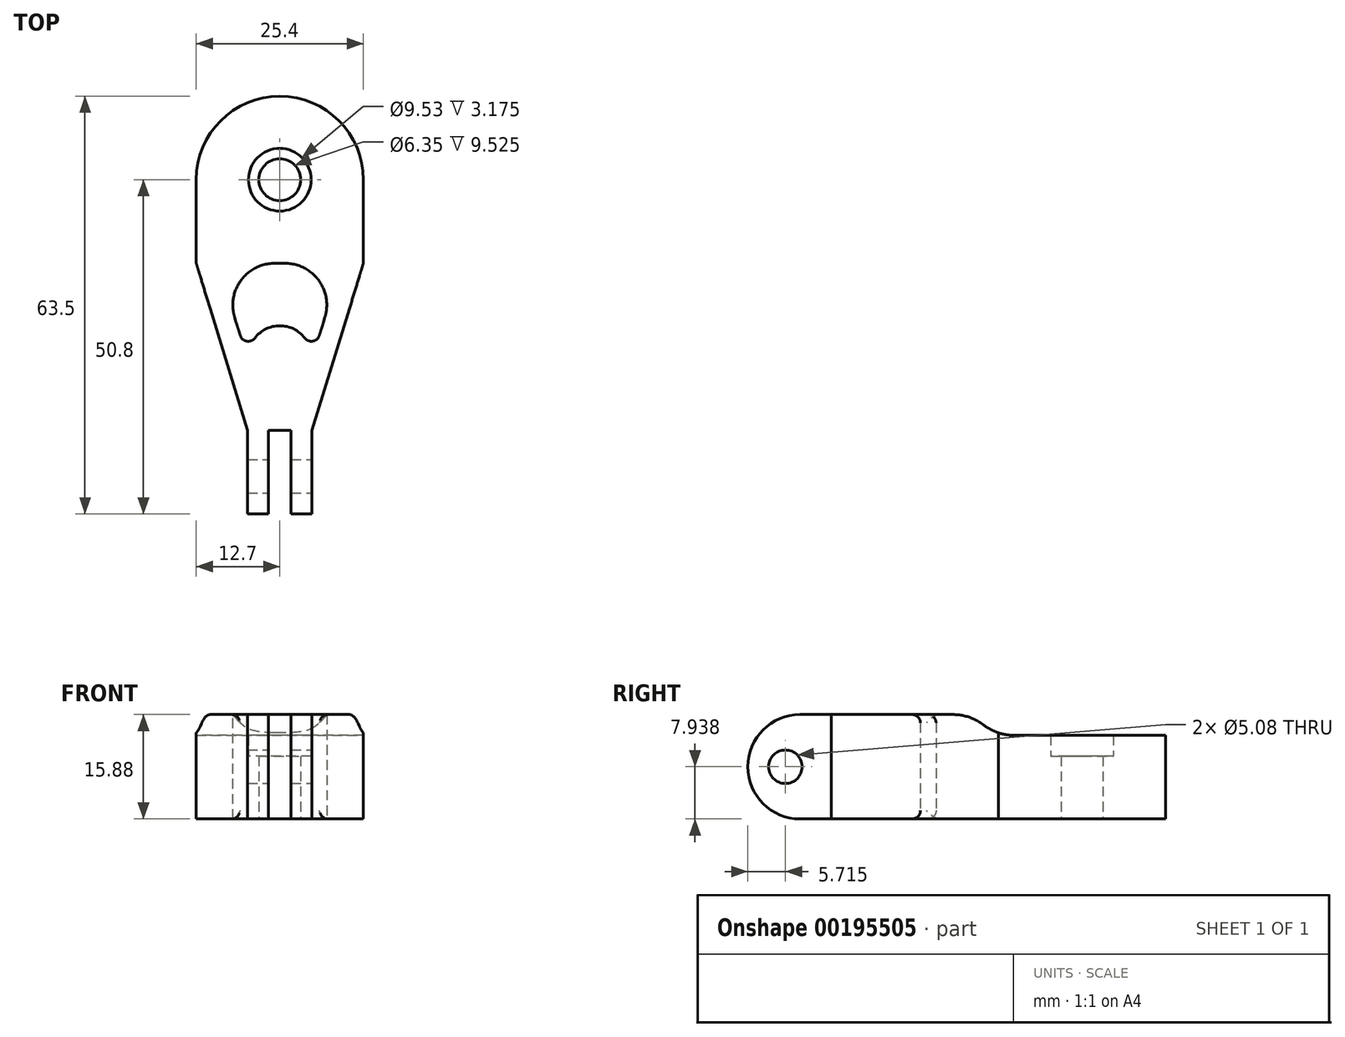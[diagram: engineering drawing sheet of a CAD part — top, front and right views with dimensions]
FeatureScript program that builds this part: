
annotation { "Feature Type Name" : "Feature", "Feature Type Description" : "" }
export const myFeature = defineFeature(function(context is Context, id is Id, definition is map)
    precondition{}
    {
        {
            var Q0;
            Q0=qCreatedBy(makeId("Top.planeOp"),FACE);
            var sketch = newSketch(context, id + "F0", { "sketchPlane" : qUnion([Q0])});
            skCircle(sketch, "E0", {"center": v(0, 0) * mm, "radius": 4.76 * mm});
            skCircle(sketch, "E1", {"center": v(0, 0) * mm, "radius": 12.7 * mm});
            skLineSegment(sketch, "E2.bottom", {"start": v(-12.7, 0) * mm, "end": v(12.7, 0) * mm});
            skLineSegment(sketch, "E2.top", {"start": v(-12.7, -50.8) * mm, "end": v(12.7, -50.8) * mm});
            skLineSegment(sketch, "E2.left", {"start": v(-12.7, 0) * mm, "end": v(-12.7, -50.8) * mm});
            skLineSegment(sketch, "E2.right", {"start": v(12.7, 0) * mm, "end": v(12.7, -50.8) * mm});
            skSolve(sketch);
        }
        {
            var Q0;
            {var subQ0=sQuery(id+"F0.wireOp",EDGE,"E2.bottom");var subQ1=sQuery(id+"F0.wireOp",EDGE,"E0");var subQ5=makeQuery(id+"F0.imprint","INTERSECT",VERTEX,{"disambiguationData":[OD(0.0)],"derivedFrom":[subQ1,subQ0]});Q0=makeQuery(id+"F0.imprint","IMPRINT",FACE,{"disambiguationData":[TD([[makeQuery(id+"F0.imprint","IMPRINT",EDGE,{"disambiguationData":[TD([[subQ5,1.0]])],"derivedFrom":subQ1}),-1.0]])]});}
            var Q1;
            {var subQ0=sQuery(id+"F0.wireOp",EDGE,"E2.bottom");var subQ1=sQuery(id+"F0.wireOp",EDGE,"E0");var subQ5=makeQuery(id+"F0.imprint","INTERSECT",VERTEX,{"disambiguationData":[OD(0.0)],"derivedFrom":[subQ1,subQ0]});Q1=makeQuery(id+"F0.imprint","IMPRINT",FACE,{"disambiguationData":[TD([[makeQuery(id+"F0.imprint","IMPRINT",EDGE,{"disambiguationData":[TD([[subQ5,-1.0]])],"derivedFrom":subQ1}),-1.0]])]});}
            var Q2;
            Q2=makeQuery(id+"F0.imprint","IMPRINT",FACE,{"disambiguationData":[TD([[makeQuery(id+"F0.imprint","IMPRINT",EDGE,{"derivedFrom":sQuery(id+"F0.wireOp",EDGE,"E2.top")}),1.0]])]});
            extrude(context, id + "F1", {"entities" : qUnion([Q0, Q1, Q2]), "depth" : 15.88 * mm});
        }
        {
            var Q0;
            Q0=qCreatedBy(makeId("Right.planeOp"),FACE);
            var sketch = newSketch(context, id + "F2", { "sketchPlane" : qUnion([Q0])});
            skLineSegment(sketch, "E3", {"start": v(12.7, 12.7) * mm, "end": v(-12.7, 12.7) * mm});
            skLineSegment(sketch, "E4", {"start": v(-12.7, 12.7) * mm, "end": v(-40.44, 32.12) * mm});
            skLineSegment(sketch, "E5", {"start": v(-40.44, 32.12) * mm, "end": v(12.7, 32.12) * mm});
            skLineSegment(sketch, "E6", {"start": v(12.7, 32.12) * mm, "end": v(12.7, 12.7) * mm});
            skSolve(sketch);
        }
        {
            var Q0;
            Q0=makeQuery(id+"F2.imprint","IMPRINT",FACE,{"disambiguationData":[TD([[makeQuery(id+"F2.imprint","IMPRINT",EDGE,{"derivedFrom":sQuery(id+"F2.wireOp",EDGE,"E3")}),-1.0]])]});
            extrude(context, id + "F3", {"entities" : qUnion([Q0]), "operationType" : NewBodyOperationType.REMOVE, "endBound" : BoundingType.SYMMETRIC, "oppositeDirection" : true, "depth" : 25.4 * mm});
        }
        {
            var Q0;
            Q0=makeQuery(id+"F1.opExtrude","CAP_FACE",FACE,{"disambiguationData":[OSD([sQuery(id+"F0.wireOp",EDGE,"E0"),sQuery(id+"F0.wireOp",EDGE,"E1"),sQuery(id+"F0.wireOp",EDGE,"E2.top"),sQuery(id+"F0.wireOp",EDGE,"E2.left"),sQuery(id+"F0.wireOp",EDGE,"E2.right")])],"isStart":false});
            var sketch = newSketch(context, id + "F4", { "sketchPlane" : qUnion([Q0])});
            skLineSegment(sketch, "E7.bottom", {"start": v(-4.9, -38.1) * mm, "end": v(-1.73, -38.1) * mm});
            skLineSegment(sketch, "E7.top", {"start": v(-4.9, -50.8) * mm, "end": v(-1.73, -50.8) * mm});
            skLineSegment(sketch, "E7.left", {"start": v(-4.9, -38.1) * mm, "end": v(-4.9, -50.8) * mm});
            skLineSegment(sketch, "E7.right", {"start": v(-1.73, -38.1) * mm, "end": v(-1.73, -50.8) * mm});
            skLineSegment(sketch, "E8.bottom", {"start": v(1.73, -38.1) * mm, "end": v(4.9, -38.1) * mm});
            skLineSegment(sketch, "E8.top", {"start": v(1.73, -50.8) * mm, "end": v(4.9, -50.8) * mm});
            skLineSegment(sketch, "E8.left", {"start": v(1.73, -38.1) * mm, "end": v(1.73, -50.8) * mm});
            skLineSegment(sketch, "E8.right", {"start": v(4.9, -38.1) * mm, "end": v(4.9, -50.8) * mm});
            skLineSegment(sketch, "E9.0.0", {"start": v(12.7, -50.8) * mm, "end": v(12.7, -17.23) * mm});
            skLineSegment(sketch, "E9.0.1", {"start": v(12.7, -17.23) * mm, "end": v(-12.7, -17.23) * mm});
            skLineSegment(sketch, "E9.0.2", {"start": v(-12.7, -17.23) * mm, "end": v(-12.7, -50.8) * mm});
            skLineSegment(sketch, "E9.0.3", {"start": v(-12.7, -50.8) * mm, "end": v(12.7, -50.8) * mm});
            skLineSegment(sketch, "E10", {"start": v(-1.73, -38.1) * mm, "end": v(1.73, -38.1) * mm});
            skLineSegment(sketch, "E11", {"start": v(4.9, -38.1) * mm, "end": v(12.7, -38.1) * mm});
            skLineSegment(sketch, "E12", {"start": v(-4.9, -38.1) * mm, "end": v(-12.7, -38.1) * mm});
            skSolve(sketch);
        }
        {
            var Q0;
            {var subQ2=sQuery(id+"F4.wireOp",EDGE,"E7.left");Q0=makeQuery(id+"F4.imprint","IMPRINT",FACE,{"disambiguationData":[TD([[makeQuery(id+"F4.imprint","IMPRINT",EDGE,{"derivedFrom":subQ2}),-1.0]])]});}
            var Q1;
            {var subQ2=sQuery(id+"F4.wireOp",EDGE,"E7.right");Q1=makeQuery(id+"F4.imprint","IMPRINT",FACE,{"disambiguationData":[TD([[makeQuery(id+"F4.imprint","IMPRINT",EDGE,{"derivedFrom":subQ2}),1.0]])]});}
            var Q2;
            {var subQ2=sQuery(id+"F4.wireOp",EDGE,"E8.right");Q2=makeQuery(id+"F4.imprint","IMPRINT",FACE,{"disambiguationData":[TD([[makeQuery(id+"F4.imprint","IMPRINT",EDGE,{"derivedFrom":subQ2}),1.0]])]});}
            extrude(context, id + "F5", {"entities" : qUnion([Q0, Q1, Q2]), "operationType" : NewBodyOperationType.REMOVE, "oppositeDirection" : true, "depth" : 25.4 * mm});
        }
        {
            var Q0;
            Q0=makeQuery(id+"F5.boolean.opBoolean","COPY",FACE,{"derivedFrom":makeQuery(id+"F5.opExtrude","SWEPT_FACE",FACE,{"disambiguationData":[OSD([sQuery(id+"F4.wireOp",EDGE,"E8.right")])]})});
            var sketch = newSketch(context, id + "F6", { "sketchPlane" : qUnion([Q0])});
            skCircle(sketch, "E13", {"center": v(-45.09, 7.94) * mm, "radius": 2.54 * mm});
            skSolve(sketch);
        }
        {
            var Q0;
            Q0=qSketchRegion(id+"F6",true);
            extrude(context, id + "F7", {"entities" : qUnion([Q0]), "operationType" : NewBodyOperationType.REMOVE, "oppositeDirection" : true, "depth" : 25.4 * mm});
        }
        {
            var Q0;
            {var subQ0=sQuery(id+"F0.wireOp",EDGE,"E2.top");Q0=makeQuery(id+"F5.boolean.opBoolean","SPLIT",EDGE,{"disambiguationData":[TD([makeQuery(id+"F5.opExtrude","SWEPT_FACE",FACE,{"disambiguationData":[OSD([sQuery(id+"F4.wireOp",EDGE,"E8.left")])]})])],"derivedFrom":makeQuery(id+"F1.opExtrude","CAP_EDGE",EDGE,{"disambiguationData":[OSD([subQ0])],"isStart":false})});}
            var Q1;
            {var subQ0=sQuery(id+"F0.wireOp",EDGE,"E2.top");Q1=makeQuery(id+"F5.boolean.opBoolean","SPLIT",EDGE,{"disambiguationData":[TD([makeQuery(id+"F5.opExtrude","SWEPT_FACE",FACE,{"disambiguationData":[OSD([sQuery(id+"F4.wireOp",EDGE,"E7.left")])]})])],"derivedFrom":makeQuery(id+"F1.opExtrude","CAP_EDGE",EDGE,{"disambiguationData":[OSD([subQ0])],"isStart":false})});}
            var Q2;
            {var subQ0=sQuery(id+"F0.wireOp",EDGE,"E2.top");Q2=makeQuery(id+"F5.boolean.opBoolean","SPLIT",EDGE,{"disambiguationData":[TD([makeQuery(id+"F5.opExtrude","SWEPT_FACE",FACE,{"disambiguationData":[OSD([sQuery(id+"F4.wireOp",EDGE,"E7.left")])]})])],"derivedFrom":makeQuery(id+"F1.opExtrude","CAP_EDGE",EDGE,{"disambiguationData":[OSD([subQ0])],"isStart":true})});}
            var Q3;
            {var subQ0=sQuery(id+"F0.wireOp",EDGE,"E2.top");Q3=makeQuery(id+"F5.boolean.opBoolean","SPLIT",EDGE,{"disambiguationData":[TD([makeQuery(id+"F5.opExtrude","SWEPT_FACE",FACE,{"disambiguationData":[OSD([sQuery(id+"F4.wireOp",EDGE,"E8.left")])]})])],"derivedFrom":makeQuery(id+"F1.opExtrude","CAP_EDGE",EDGE,{"disambiguationData":[OSD([subQ0])],"isStart":true})});}
            fillet(context, id + "F8", {"entities" : qUnion([Q0, Q1, Q2, Q3]), "radius" : 7.94 * mm, "tangentPropagation" : true, "allowEdgeOverflow" : false});
        }
        {
            var Q0;
            Q0=qCreatedBy(makeId("Top.planeOp"),FACE);
            var sketch = newSketch(context, id + "F9", { "sketchPlane" : qUnion([Q0])});
            skLineSegment(sketch, "E14.0.0", {"start": v(-1.73, -38.1) * mm, "end": v(-1.73, -42.86) * mm});
            skLineSegment(sketch, "E14.0.1", {"start": v(-1.73, -42.86) * mm, "end": v(-4.9, -42.86) * mm});
            skLineSegment(sketch, "E14.0.2", {"start": v(-4.9, -42.86) * mm, "end": v(-4.9, -38.1) * mm});
            skLineSegment(sketch, "E14.0.3", {"start": v(-4.9, -38.1) * mm, "end": v(-12.7, -38.1) * mm});
            skLineSegment(sketch, "E14.0.4", {"start": v(-12.7, -38.1) * mm, "end": v(-12.7, 0) * mm});
            skArc(sketch, "E14.0.5", {"start": v(-12.7, 0) * mm, "mid": v(0, 12.7) * mm, "end": v(12.7, 0) * mm});
            skLineSegment(sketch, "E14.0.6", {"start": v(12.7, 0) * mm, "end": v(12.7, -38.1) * mm});
            skLineSegment(sketch, "E14.0.7", {"start": v(12.7, -38.1) * mm, "end": v(4.9, -38.1) * mm});
            skLineSegment(sketch, "E14.0.8", {"start": v(4.9, -38.1) * mm, "end": v(4.9, -42.86) * mm});
            skLineSegment(sketch, "E14.0.9", {"start": v(4.9, -42.86) * mm, "end": v(1.73, -42.86) * mm});
            skLineSegment(sketch, "E14.0.10", {"start": v(1.73, -42.86) * mm, "end": v(1.73, -38.1) * mm});
            skLineSegment(sketch, "E14.0.11", {"start": v(1.73, -38.1) * mm, "end": v(-1.73, -38.1) * mm});
            skLineSegment(sketch, "E15", {"start": v(4.9, -38.1) * mm, "end": v(12.7, -12.7) * mm});
            skLineSegment(sketch, "E16", {"start": v(-4.9, -38.1) * mm, "end": v(-12.7, -12.7) * mm});
            skSolve(sketch);
        }
        {
            var Q0;
            {var subQ2=sQuery(id+"F9.wireOp",EDGE,"E14.0.3");Q0=makeQuery(id+"F9.imprint","IMPRINT",FACE,{"disambiguationData":[TD([[makeQuery(id+"F9.imprint","IMPRINT",EDGE,{"derivedFrom":subQ2}),-1.0]])]});}
            var Q1;
            {var subQ1=sQuery(id+"F9.wireOp",EDGE,"E14.0.7");Q1=makeQuery(id+"F9.imprint","IMPRINT",FACE,{"disambiguationData":[TD([[makeQuery(id+"F9.imprint","IMPRINT",EDGE,{"derivedFrom":subQ1}),-1.0]])]});}
            extrude(context, id + "F10", {"entities" : qUnion([Q0, Q1]), "operationType" : NewBodyOperationType.REMOVE, "depth" : 25.4 * mm});
        }
        {
            var Q0;
            Q0=makeQuery(id+"F1.opExtrude","CAP_FACE",FACE,{"disambiguationData":[OSD([sQuery(id+"F0.wireOp",EDGE,"E0"),sQuery(id+"F0.wireOp",EDGE,"E1"),sQuery(id+"F0.wireOp",EDGE,"E2.top"),sQuery(id+"F0.wireOp",EDGE,"E2.left"),sQuery(id+"F0.wireOp",EDGE,"E2.right")])],"isStart":true});
            var sketch = newSketch(context, id + "F11", { "sketchPlane" : qUnion([Q0])});
            skLineSegment(sketch, "E17.0.0", {"start": v(-4.9, 38.1) * mm, "end": v(-12.7, 12.7) * mm});
            skLineSegment(sketch, "E17.0.1", {"start": v(-12.7, 12.7) * mm, "end": v(-12.7, 0) * mm});
            skArc(sketch, "E17.0.2", {"start": v(-12.7, 0) * mm, "mid": v(0, -12.7) * mm, "end": v(12.7, 0) * mm});
            skLineSegment(sketch, "E17.0.3", {"start": v(12.7, 0) * mm, "end": v(12.7, 12.7) * mm});
            skLineSegment(sketch, "E17.0.4", {"start": v(12.7, 12.7) * mm, "end": v(4.9, 38.1) * mm});
            skLineSegment(sketch, "E17.0.5", {"start": v(4.9, 38.1) * mm, "end": v(4.9, 42.86) * mm});
            skLineSegment(sketch, "E17.0.6", {"start": v(4.9, 42.86) * mm, "end": v(1.73, 42.86) * mm});
            skLineSegment(sketch, "E17.0.7", {"start": v(1.73, 42.86) * mm, "end": v(1.73, 38.1) * mm});
            skLineSegment(sketch, "E17.0.8", {"start": v(1.73, 38.1) * mm, "end": v(-1.73, 38.1) * mm});
            skLineSegment(sketch, "E17.0.9", {"start": v(-1.73, 38.1) * mm, "end": v(-1.73, 42.86) * mm});
            skLineSegment(sketch, "E17.0.10", {"start": v(-1.73, 42.86) * mm, "end": v(-4.9, 42.86) * mm});
            skLineSegment(sketch, "E17.0.11", {"start": v(-4.9, 42.86) * mm, "end": v(-4.9, 38.1) * mm});
            skLineSegment(sketch, "E18", {"start": v(0, 31.75) * mm, "end": v(0, 12.7) * mm});
            skLineSegment(sketch, "E19", {"start": v(12.7, 12.7) * mm, "end": v(0, 12.7) * mm});
            skCircle(sketch, "E20", {"center": v(0, 26.97) * mm, "radius": 4.78 * mm});
            skLineSegment(sketch, "E21", {"start": v(9.38, 12.7) * mm, "end": v(4.57, 28.38) * mm});
            skLineSegment(sketch, "E22", {"start": v(0, 12.7) * mm, "end": v(-12.7, 12.7) * mm});
            skLineSegment(sketch, "E23", {"start": v(-9.38, 12.7) * mm, "end": v(-4.57, 28.38) * mm});
            skSolve(sketch);
        }
        {
            var Q0;
            {var subQ0=sQuery(id+"F11.wireOp",EDGE,"E20");var subQ1=sQuery(id+"F11.wireOp",EDGE,"E18");var subQ4=makeQuery(id+"F11.imprint","INTERSECT",VERTEX,{"disambiguationData":[OD(0.0)],"derivedFrom":[subQ1,subQ0]});Q0=makeQuery(id+"F11.imprint","IMPRINT",FACE,{"disambiguationData":[TD([[makeQuery(id+"F11.imprint","IMPRINT",EDGE,{"disambiguationData":[TD([[subQ4,-1.0]])],"derivedFrom":subQ1}),-1.0]])]});}
            var Q1;
            {var subQ0=sQuery(id+"F11.wireOp",EDGE,"E20");var subQ1=sQuery(id+"F11.wireOp",EDGE,"E18");var subQ4=makeQuery(id+"F11.imprint","INTERSECT",VERTEX,{"disambiguationData":[OD(0.0)],"derivedFrom":[subQ1,subQ0]});Q1=makeQuery(id+"F11.imprint","IMPRINT",FACE,{"disambiguationData":[TD([[makeQuery(id+"F11.imprint","IMPRINT",EDGE,{"disambiguationData":[TD([[subQ4,-1.0]])],"derivedFrom":subQ1}),1.0]])]});}
            var Q2;
            {var subQ0=sQuery(id+"F11.wireOp",EDGE,"E21");Q2=makeQuery(id+"F11.imprint","IMPRINT",FACE,{"disambiguationData":[TD([[makeQuery(id+"F11.imprint","IMPRINT",EDGE,{"derivedFrom":subQ0}),1.0]])]});}
            var Q3;
            {var subQ0=sQuery(id+"F11.wireOp",EDGE,"E23");Q3=makeQuery(id+"F11.imprint","IMPRINT",FACE,{"disambiguationData":[TD([[makeQuery(id+"F11.imprint","IMPRINT",EDGE,{"derivedFrom":subQ0}),-1.0]])]});}
            extrude(context, id + "F12", {"entities" : qUnion([Q0, Q1, Q2, Q3]), "operationType" : NewBodyOperationType.REMOVE, "oppositeDirection" : true, "depth" : 25.4 * mm});
        }
        {
            var Q0;
            Q0=makeQuery(id+"F12.boolean.opBoolean","COPY",EDGE,{"derivedFrom":makeQuery(id+"F12.opExtrude","SWEPT_EDGE",EDGE,{"disambiguationData":[OSD([sQuery(id+"F11.wireOp",EDGE,"E22"),sQuery(id+"F11.wireOp",EDGE,"E23")])]})});
            var Q1;
            Q1=makeQuery(id+"F12.boolean.opBoolean","COPY",EDGE,{"derivedFrom":makeQuery(id+"F12.opExtrude","SWEPT_EDGE",EDGE,{"disambiguationData":[OSD([sQuery(id+"F11.wireOp",EDGE,"E19"),sQuery(id+"F11.wireOp",EDGE,"E21")])]})});
            fillet(context, id + "F13", {"entities" : qUnion([Q0, Q1]), "radius" : 6.35 * mm, "tangentPropagation" : true, "allowEdgeOverflow" : false});
        }
        {
            var Q0;
            {var subQ0=makeQuery(id+"F1.opExtrude","CAP_FACE",FACE,{"disambiguationData":[OSD([sQuery(id+"F0.wireOp",EDGE,"E0"),sQuery(id+"F0.wireOp",EDGE,"E1"),sQuery(id+"F0.wireOp",EDGE,"E2.top"),sQuery(id+"F0.wireOp",EDGE,"E2.left"),sQuery(id+"F0.wireOp",EDGE,"E2.right")])],"isStart":false});var subQ1=makeQuery(id+"F3.opExtrude","SWEPT_FACE",FACE,{"disambiguationData":[OSD([sQuery(id+"F2.wireOp",EDGE,"E4")])]});Q0=makeQuery(id+"F12.boolean.opBoolean","SPLIT",EDGE,{"disambiguationData":[TD([makeQuery(id+"F10.boolean.opBoolean","COPY",FACE,{"derivedFrom":makeQuery(id+"F10.opExtrude","SWEPT_FACE",FACE,{"disambiguationData":[OSD([sQuery(id+"F9.wireOp",EDGE,"E15")])]})})])],"derivedFrom":makeQuery(id+"F3.boolean.opBoolean","INTERSECT",EDGE,{"derivedFrom":[subQ0,subQ1]})});}
            var Q1;
            {var subQ0=makeQuery(id+"F1.opExtrude","CAP_FACE",FACE,{"disambiguationData":[OSD([sQuery(id+"F0.wireOp",EDGE,"E0"),sQuery(id+"F0.wireOp",EDGE,"E1"),sQuery(id+"F0.wireOp",EDGE,"E2.top"),sQuery(id+"F0.wireOp",EDGE,"E2.left"),sQuery(id+"F0.wireOp",EDGE,"E2.right")])],"isStart":false});var subQ1=makeQuery(id+"F3.opExtrude","SWEPT_FACE",FACE,{"disambiguationData":[OSD([sQuery(id+"F2.wireOp",EDGE,"E4")])]});Q1=makeQuery(id+"F12.boolean.opBoolean","SPLIT",EDGE,{"disambiguationData":[TD([makeQuery(id+"F10.boolean.opBoolean","COPY",FACE,{"derivedFrom":makeQuery(id+"F10.opExtrude","SWEPT_FACE",FACE,{"disambiguationData":[OSD([sQuery(id+"F9.wireOp",EDGE,"E16")])]})})])],"derivedFrom":makeQuery(id+"F3.boolean.opBoolean","INTERSECT",EDGE,{"derivedFrom":[subQ0,subQ1]})});}
            var Q2;
            {var subQ0=sQuery(id+"F2.wireOp",EDGE,"E3");var subQ1=sQuery(id+"F2.wireOp",EDGE,"E4");Q2=makeQuery(id+"F12.boolean.opBoolean","SPLIT",EDGE,{"disambiguationData":[TD([makeQuery(id+"F1.opExtrude","SWEPT_FACE",FACE,{"disambiguationData":[OSD([sQuery(id+"F0.wireOp",EDGE,"E2.left")])]}),makeQuery(id+"F3.boolean.opBoolean","COPY",FACE,{"derivedFrom":makeQuery(id+"F3.opExtrude","SWEPT_FACE",FACE,{"disambiguationData":[OSD([subQ0])]})}),makeQuery(id+"F3.boolean.opBoolean","COPY",FACE,{"derivedFrom":makeQuery(id+"F3.opExtrude","SWEPT_FACE",FACE,{"disambiguationData":[OSD([subQ1])]})}),makeQuery(id+"F10.boolean.opBoolean","COPY",FACE,{"derivedFrom":makeQuery(id+"F10.opExtrude","SWEPT_FACE",FACE,{"disambiguationData":[OSD([sQuery(id+"F9.wireOp",EDGE,"E16")])]})}),makeQuery(id+"F12.opExtrude","SWEPT_FACE",FACE,{"disambiguationData":[OSD([sQuery(id+"F11.wireOp",EDGE,"E19"),sQuery(id+"F11.wireOp",EDGE,"E22")])]}),makeQuery(id+"F12.opExtrude","SWEPT_FACE",FACE,{"disambiguationData":[OSD([sQuery(id+"F11.wireOp",EDGE,"E23")])]})])],"derivedFrom":makeQuery(id+"F3.boolean.opBoolean","COPY",EDGE,{"derivedFrom":makeQuery(id+"F3.opExtrude","SWEPT_EDGE",EDGE,{"disambiguationData":[OSD([subQ0,subQ1])]})})});}
            fillet(context, id + "F14", {"entities" : qUnion([Q0, Q1, Q2]), "radius" : 7.62 * mm, "tangentPropagation" : true, "allowEdgeOverflow" : false});
        }
        {
            var Q0;
            Q0=makeQuery(id+"F12.boolean.opBoolean","COPY",FACE,{"derivedFrom":makeQuery(id+"F12.opExtrude","SWEPT_FACE",FACE,{"disambiguationData":[OSD([sQuery(id+"F11.wireOp",EDGE,"E20")])]})});
            fillet(context, id + "F15", {"entities" : qUnion([Q0]), "radius" : 1.27 * mm, "tangentPropagation" : true, "allowEdgeOverflow" : false});
        }
        {
            var Q0;
            Q0=makeQuery(id+"F1.opExtrude","CAP_FACE",FACE,{"disambiguationData":[OSD([sQuery(id+"F0.wireOp",EDGE,"E0"),sQuery(id+"F0.wireOp",EDGE,"E1"),sQuery(id+"F0.wireOp",EDGE,"E2.top"),sQuery(id+"F0.wireOp",EDGE,"E2.left"),sQuery(id+"F0.wireOp",EDGE,"E2.right")])],"isStart":true});
            var sketch = newSketch(context, id + "F16", { "sketchPlane" : qUnion([Q0])});
            skCircle(sketch, "E24", {"center": v(0, 0) * mm, "radius": 3.18 * mm});
            skCircle(sketch, "E25.0", {"center": v(0, 0) * mm, "radius": 4.76 * mm});
            skSolve(sketch);
        }
        {
            var Q0;
            Q0=makeQuery(id+"F16.imprint","IMPRINT",FACE,{"disambiguationData":[TD([[makeQuery(id+"F16.imprint","IMPRINT",EDGE,{"derivedFrom":sQuery(id+"F16.wireOp",EDGE,"E24")}),-1.0]])]});
            extrude(context, id + "F17", {"entities" : qUnion([Q0]), "operationType" : NewBodyOperationType.ADD, "oppositeDirection" : true, "depth" : 9.52 * mm});
        }
    });
